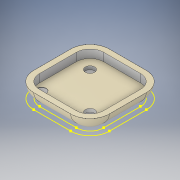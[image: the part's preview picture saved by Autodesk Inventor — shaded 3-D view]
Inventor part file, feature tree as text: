
AUTODESK INVENTOR PART (.ipt)
format: ipt  version: 2018 (Build 220112000, 112)  size: 300,032 bytes
history: native  units: in
note: dims shown in document units (in); Inventor stores cm internally (conversion verified against a paired STEP export)
features: other x6, extrude x4, projected_geometry x1
ambient origin geometry x8: Origin, YZ Plane, XZ Plane, XY Plane, X Axis, Y Axis, Z Axis, Center Point
bodies: Solid1 (feature_tree)
feature tree (11):
  other  "Case Bottom.ipt"
  extrude  "Extrusion1"  Depth=0.3937in
  extrude  "Extrusion2"  Depth=0.09in TaperAngle=0.0deg
  other  "Narrowing Sketch"
  extrude  "Extrusion4"  Depth=0.01in TaperAngle=0.0deg
  extrude  "Narrowing Extrusion"  TaperAngle=0.0deg  [1 undecoded]
  other  "Solid2::Case Bottom.ipt"
  other  "TaggingFeature1"
  other  "Alignment Sketch"
  other  "Peg Sketch"
  projected_geometry  "Projected Loop2"
note: 1 required parameter value undecoded (feature->parameter linkage not recoverable at this tier; creation-order binding heuristic only, values carry confidence <= 0.55)
